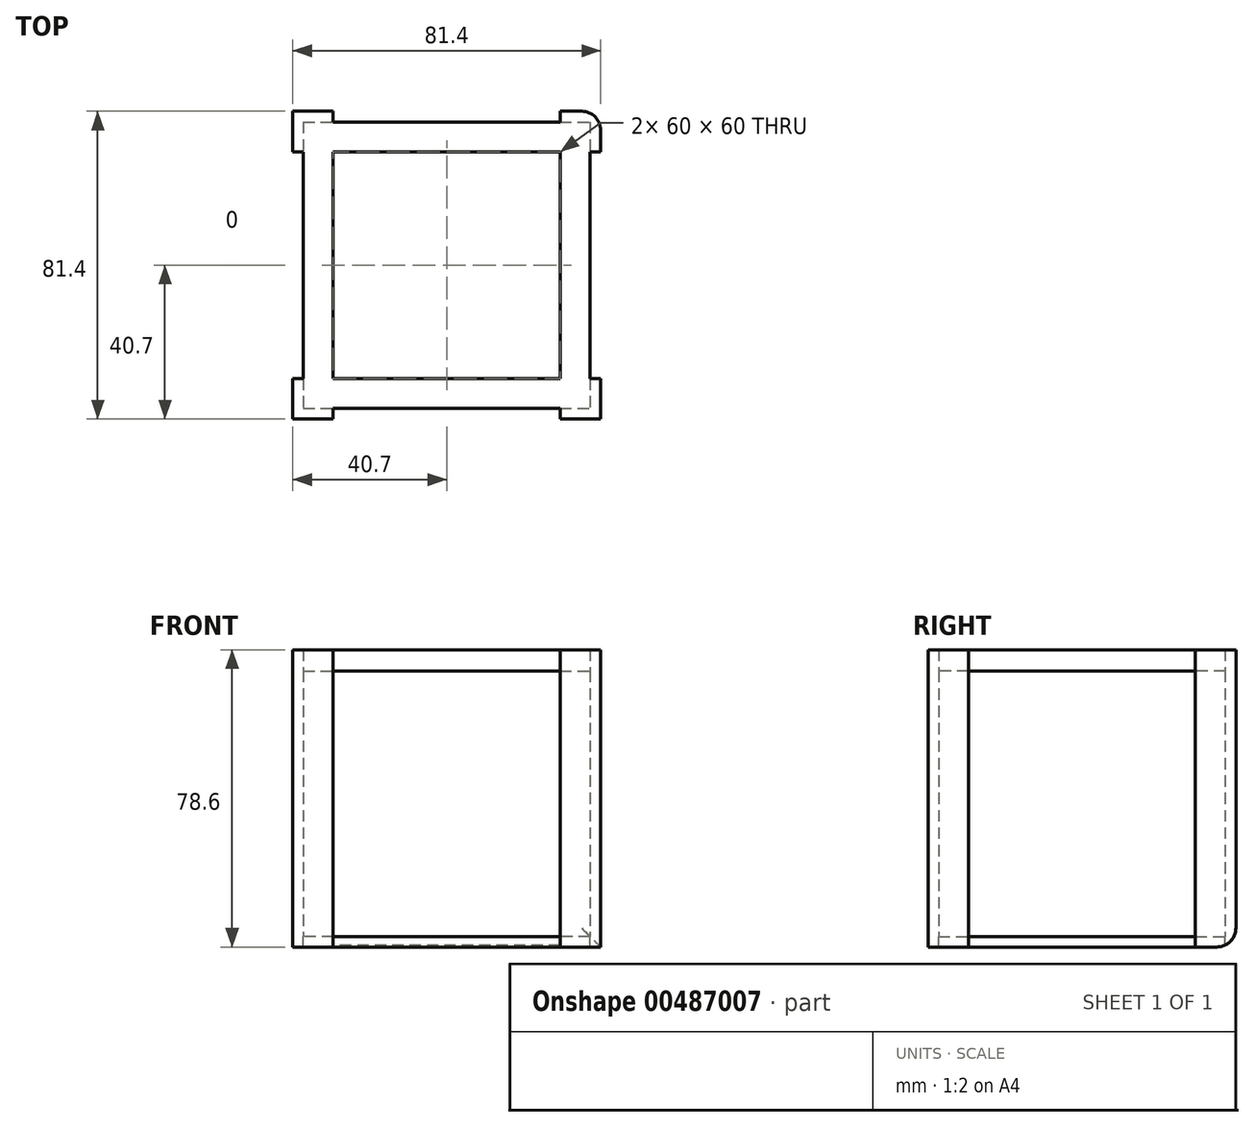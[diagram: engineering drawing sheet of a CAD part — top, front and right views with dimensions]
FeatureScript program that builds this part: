
annotation { "Feature Type Name" : "Feature", "Feature Type Description" : "" }
export const myFeature = defineFeature(function(context is Context, id is Id, definition is map)
    precondition{}
    {
        {
            var Q0;
            Q0=qCreatedBy(makeId("Top.planeOp"),FACE);
            var sketch = newSketch(context, id + "F0", { "sketchPlane" : qUnion([Q0])});
            skLineSegment(sketch, "E0.bottom", {"start": v(37.9, -37.9) * mm, "end": v(-37.9, -37.9) * mm});
            skLineSegment(sketch, "E0.top", {"start": v(37.9, 37.9) * mm, "end": v(-37.9, 37.9) * mm});
            skLineSegment(sketch, "E0.left", {"start": v(37.9, -37.9) * mm, "end": v(37.9, 37.9) * mm});
            skLineSegment(sketch, "E0.right", {"start": v(-37.9, -37.9) * mm, "end": v(-37.9, 37.9) * mm});
            skPoint(sketch, "E0.middle", {"position": v(0, 0) * mm});
            skLineSegment(sketch, "E1.0", {"start": v(40.7, 40.7) * mm, "end": v(-40.7, 40.7) * mm});
            skLineSegment(sketch, "E1.1", {"start": v(40.7, -40.7) * mm, "end": v(40.7, 40.7) * mm});
            skLineSegment(sketch, "E1.2", {"start": v(40.7, -40.7) * mm, "end": v(-40.7, -40.7) * mm});
            skLineSegment(sketch, "E1.3", {"start": v(-40.7, -40.7) * mm, "end": v(-40.7, 40.7) * mm});
            skLineSegment(sketch, "E2.bottom", {"start": v(-30, 40.7) * mm, "end": v(30, 40.7) * mm});
            skLineSegment(sketch, "E2.top", {"start": v(-30, -40.7) * mm, "end": v(30, -40.7) * mm});
            skLineSegment(sketch, "E2.left", {"start": v(-30, 40.7) * mm, "end": v(-30, -40.7) * mm});
            skLineSegment(sketch, "E2.right", {"start": v(30, 40.7) * mm, "end": v(30, -40.7) * mm});
            skLineSegment(sketch, "E3.bottom", {"start": v(-40.7, 30) * mm, "end": v(40.7, 30) * mm});
            skLineSegment(sketch, "E3.top", {"start": v(-40.7, -30) * mm, "end": v(40.7, -30) * mm});
            skLineSegment(sketch, "E3.left", {"start": v(-40.7, 30) * mm, "end": v(-40.7, -30) * mm});
            skLineSegment(sketch, "E3.right", {"start": v(40.7, 30) * mm, "end": v(40.7, -30) * mm});
            skSolve(sketch);
        }
        {
            var Q0;
            {var subQ5=sQuery(id+"F0.wireOp",EDGE,"E2.bottom");Q0=makeQuery(id+"F0.imprint","IMPRINT",FACE,{"disambiguationData":[TD([[makeQuery(id+"F0.imprint","IMPRINT",EDGE,{"derivedFrom":subQ5}),-1.0]])]});}
            var Q1;
            {var subQ7=sQuery(id+"F0.wireOp",EDGE,"E0.right");var subQ8=sQuery(id+"F0.wireOp",EDGE,"E0.top");var subQ9=makeQuery(id+"F0.imprint","INTERSECT",VERTEX,{"derivedFrom":[subQ8,subQ7]});Q1=makeQuery(id+"F0.imprint","IMPRINT",FACE,{"disambiguationData":[TD([[makeQuery(id+"F0.imprint","IMPRINT",EDGE,{"disambiguationData":[TD([[subQ9,1.0]])],"derivedFrom":subQ8}),-1.0]])]});}
            var Q2;
            {var subQ7=sQuery(id+"F0.wireOp",EDGE,"E0.left");var subQ8=sQuery(id+"F0.wireOp",EDGE,"E0.top");var subQ9=makeQuery(id+"F0.imprint","INTERSECT",VERTEX,{"derivedFrom":[subQ8,subQ7]});Q2=makeQuery(id+"F0.imprint","IMPRINT",FACE,{"disambiguationData":[TD([[makeQuery(id+"F0.imprint","IMPRINT",EDGE,{"disambiguationData":[TD([[subQ9,-1.0]])],"derivedFrom":subQ8}),-1.0]])]});}
            var Q3;
            {var subQ5=sQuery(id+"F0.wireOp",EDGE,"E3.right");Q3=makeQuery(id+"F0.imprint","IMPRINT",FACE,{"disambiguationData":[TD([[makeQuery(id+"F0.imprint","IMPRINT",EDGE,{"derivedFrom":subQ5}),-1.0]])]});}
            var Q4;
            {var subQ7=sQuery(id+"F0.wireOp",EDGE,"E0.left");var subQ8=sQuery(id+"F0.wireOp",EDGE,"E0.bottom");var subQ9=makeQuery(id+"F0.imprint","INTERSECT",VERTEX,{"derivedFrom":[subQ8,subQ7]});Q4=makeQuery(id+"F0.imprint","IMPRINT",FACE,{"disambiguationData":[TD([[makeQuery(id+"F0.imprint","IMPRINT",EDGE,{"disambiguationData":[TD([[subQ9,-1.0]])],"derivedFrom":subQ8}),1.0]])]});}
            var Q5;
            {var subQ5=sQuery(id+"F0.wireOp",EDGE,"E2.top");Q5=makeQuery(id+"F0.imprint","IMPRINT",FACE,{"disambiguationData":[TD([[makeQuery(id+"F0.imprint","IMPRINT",EDGE,{"derivedFrom":subQ5}),1.0]])]});}
            var Q6;
            {var subQ5=sQuery(id+"F0.wireOp",EDGE,"E0.right");var subQ6=sQuery(id+"F0.wireOp",EDGE,"E0.bottom");var subQ7=makeQuery(id+"F0.imprint","INTERSECT",VERTEX,{"derivedFrom":[subQ6,subQ5]});Q6=makeQuery(id+"F0.imprint","IMPRINT",FACE,{"disambiguationData":[TD([[makeQuery(id+"F0.imprint","IMPRINT",EDGE,{"disambiguationData":[TD([[subQ7,1.0]])],"derivedFrom":subQ6}),1.0]])]});}
            var Q7;
            {var subQ5=sQuery(id+"F0.wireOp",EDGE,"E3.left");Q7=makeQuery(id+"F0.imprint","IMPRINT",FACE,{"disambiguationData":[TD([[makeQuery(id+"F0.imprint","IMPRINT",EDGE,{"derivedFrom":subQ5}),1.0]])]});}
            var Q8;
            {var subQ0=sQuery(id+"F0.wireOp",EDGE,"E0.left");var subQ1=sQuery(id+"F0.wireOp",EDGE,"E0.bottom");var subQ2=makeQuery(id+"F0.imprint","INTERSECT",VERTEX,{"derivedFrom":[subQ1,subQ0]});Q8=makeQuery(id+"F0.imprint","IMPRINT",FACE,{"disambiguationData":[TD([[makeQuery(id+"F0.imprint","IMPRINT",EDGE,{"disambiguationData":[TD([[subQ2,-1.0]])],"derivedFrom":subQ1}),-1.0]])]});}
            var Q9;
            {var subQ0=sQuery(id+"F0.wireOp",EDGE,"E0.left");var subQ1=sQuery(id+"F0.wireOp",EDGE,"E0.top");var subQ2=makeQuery(id+"F0.imprint","INTERSECT",VERTEX,{"derivedFrom":[subQ1,subQ0]});Q9=makeQuery(id+"F0.imprint","IMPRINT",FACE,{"disambiguationData":[TD([[makeQuery(id+"F0.imprint","IMPRINT",EDGE,{"disambiguationData":[TD([[subQ2,-1.0]])],"derivedFrom":subQ1}),1.0]])]});}
            var Q10;
            {var subQ0=sQuery(id+"F0.wireOp",EDGE,"E0.right");var subQ1=sQuery(id+"F0.wireOp",EDGE,"E0.top");var subQ2=makeQuery(id+"F0.imprint","INTERSECT",VERTEX,{"derivedFrom":[subQ1,subQ0]});Q10=makeQuery(id+"F0.imprint","IMPRINT",FACE,{"disambiguationData":[TD([[makeQuery(id+"F0.imprint","IMPRINT",EDGE,{"disambiguationData":[TD([[subQ2,1.0]])],"derivedFrom":subQ1}),1.0]])]});}
            var Q11;
            {var subQ0=sQuery(id+"F0.wireOp",EDGE,"E3.top");var subQ1=sQuery(id+"F0.wireOp",EDGE,"E0.right");var subQ2=makeQuery(id+"F0.imprint","INTERSECT",VERTEX,{"derivedFrom":[subQ1,subQ0]});Q11=makeQuery(id+"F0.imprint","IMPRINT",FACE,{"disambiguationData":[TD([[makeQuery(id+"F0.imprint","IMPRINT",EDGE,{"disambiguationData":[TD([[subQ2,-1.0]])],"derivedFrom":subQ1}),-1.0]])]});}
            var Q12;
            {var subQ0=sQuery(id+"F0.wireOp",EDGE,"E3.top");var subQ1=sQuery(id+"F0.wireOp",EDGE,"E0.left");var subQ2=makeQuery(id+"F0.imprint","INTERSECT",VERTEX,{"derivedFrom":[subQ1,subQ0]});Q12=makeQuery(id+"F0.imprint","IMPRINT",FACE,{"disambiguationData":[TD([[makeQuery(id+"F0.imprint","IMPRINT",EDGE,{"disambiguationData":[TD([[subQ2,-1.0]])],"derivedFrom":subQ1}),1.0]])]});}
            var Q13;
            {var subQ0=sQuery(id+"F0.wireOp",EDGE,"E0.right");var subQ1=sQuery(id+"F0.wireOp",EDGE,"E0.bottom");var subQ2=makeQuery(id+"F0.imprint","INTERSECT",VERTEX,{"derivedFrom":[subQ1,subQ0]});Q13=makeQuery(id+"F0.imprint","IMPRINT",FACE,{"disambiguationData":[TD([[makeQuery(id+"F0.imprint","IMPRINT",EDGE,{"disambiguationData":[TD([[subQ2,1.0]])],"derivedFrom":subQ1}),-1.0]])]});}
            var Q14;
            {var subQ0=sQuery(id+"F0.wireOp",EDGE,"E2.right");var subQ1=sQuery(id+"F0.wireOp",EDGE,"E0.bottom");var subQ2=makeQuery(id+"F0.imprint","INTERSECT",VERTEX,{"derivedFrom":[subQ1,subQ0]});Q14=makeQuery(id+"F0.imprint","IMPRINT",FACE,{"disambiguationData":[TD([[makeQuery(id+"F0.imprint","IMPRINT",EDGE,{"disambiguationData":[TD([[subQ2,-1.0]])],"derivedFrom":subQ1}),-1.0]])]});}
            var Q15;
            {var subQ0=sQuery(id+"F0.wireOp",EDGE,"E2.right");var subQ1=sQuery(id+"F0.wireOp",EDGE,"E0.top");var subQ2=makeQuery(id+"F0.imprint","INTERSECT",VERTEX,{"derivedFrom":[subQ1,subQ0]});Q15=makeQuery(id+"F0.imprint","IMPRINT",FACE,{"disambiguationData":[TD([[makeQuery(id+"F0.imprint","IMPRINT",EDGE,{"disambiguationData":[TD([[subQ2,-1.0]])],"derivedFrom":subQ1}),1.0]])]});}
            extrude(context, id + "F1", {"entities" : qUnion([Q0, Q1, Q2, Q3, Q4, Q5, Q6, Q7, Q8, Q9, Q10, Q11, Q12, Q13, Q14, Q15]), "depth" : 75.8 * mm});
        }
        {
            var Q0;
            {var subQ7=sQuery(id+"F0.wireOp",EDGE,"E0.right");var subQ8=sQuery(id+"F0.wireOp",EDGE,"E0.top");var subQ9=makeQuery(id+"F0.imprint","INTERSECT",VERTEX,{"derivedFrom":[subQ8,subQ7]});Q0=makeQuery(id+"F0.imprint","IMPRINT",FACE,{"disambiguationData":[TD([[makeQuery(id+"F0.imprint","IMPRINT",EDGE,{"disambiguationData":[TD([[subQ9,1.0]])],"derivedFrom":subQ8}),-1.0]])]});}
            var Q1;
            {var subQ0=sQuery(id+"F0.wireOp",EDGE,"E0.right");var subQ1=sQuery(id+"F0.wireOp",EDGE,"E0.top");var subQ2=makeQuery(id+"F0.imprint","INTERSECT",VERTEX,{"derivedFrom":[subQ1,subQ0]});Q1=makeQuery(id+"F0.imprint","IMPRINT",FACE,{"disambiguationData":[TD([[makeQuery(id+"F0.imprint","IMPRINT",EDGE,{"disambiguationData":[TD([[subQ2,1.0]])],"derivedFrom":subQ1}),1.0]])]});}
            var Q2;
            {var subQ5=sQuery(id+"F0.wireOp",EDGE,"E3.left");Q2=makeQuery(id+"F0.imprint","IMPRINT",FACE,{"disambiguationData":[TD([[makeQuery(id+"F0.imprint","IMPRINT",EDGE,{"derivedFrom":subQ5}),1.0]])]});}
            var Q3;
            {var subQ0=sQuery(id+"F0.wireOp",EDGE,"E3.top");var subQ1=sQuery(id+"F0.wireOp",EDGE,"E0.right");var subQ2=makeQuery(id+"F0.imprint","INTERSECT",VERTEX,{"derivedFrom":[subQ1,subQ0]});Q3=makeQuery(id+"F0.imprint","IMPRINT",FACE,{"disambiguationData":[TD([[makeQuery(id+"F0.imprint","IMPRINT",EDGE,{"disambiguationData":[TD([[subQ2,-1.0]])],"derivedFrom":subQ1}),-1.0]])]});}
            var Q4;
            {var subQ5=sQuery(id+"F0.wireOp",EDGE,"E0.right");var subQ6=sQuery(id+"F0.wireOp",EDGE,"E0.bottom");var subQ7=makeQuery(id+"F0.imprint","INTERSECT",VERTEX,{"derivedFrom":[subQ6,subQ5]});Q4=makeQuery(id+"F0.imprint","IMPRINT",FACE,{"disambiguationData":[TD([[makeQuery(id+"F0.imprint","IMPRINT",EDGE,{"disambiguationData":[TD([[subQ7,1.0]])],"derivedFrom":subQ6}),1.0]])]});}
            var Q5;
            {var subQ0=sQuery(id+"F0.wireOp",EDGE,"E0.right");var subQ1=sQuery(id+"F0.wireOp",EDGE,"E0.bottom");var subQ2=makeQuery(id+"F0.imprint","INTERSECT",VERTEX,{"derivedFrom":[subQ1,subQ0]});Q5=makeQuery(id+"F0.imprint","IMPRINT",FACE,{"disambiguationData":[TD([[makeQuery(id+"F0.imprint","IMPRINT",EDGE,{"disambiguationData":[TD([[subQ2,1.0]])],"derivedFrom":subQ1}),-1.0]])]});}
            var Q6;
            {var subQ5=sQuery(id+"F0.wireOp",EDGE,"E2.top");Q6=makeQuery(id+"F0.imprint","IMPRINT",FACE,{"disambiguationData":[TD([[makeQuery(id+"F0.imprint","IMPRINT",EDGE,{"derivedFrom":subQ5}),1.0]])]});}
            var Q7;
            {var subQ0=sQuery(id+"F0.wireOp",EDGE,"E0.left");var subQ1=sQuery(id+"F0.wireOp",EDGE,"E0.bottom");var subQ2=makeQuery(id+"F0.imprint","INTERSECT",VERTEX,{"derivedFrom":[subQ1,subQ0]});Q7=makeQuery(id+"F0.imprint","IMPRINT",FACE,{"disambiguationData":[TD([[makeQuery(id+"F0.imprint","IMPRINT",EDGE,{"disambiguationData":[TD([[subQ2,-1.0]])],"derivedFrom":subQ1}),-1.0]])]});}
            var Q8;
            {var subQ0=sQuery(id+"F0.wireOp",EDGE,"E3.top");var subQ1=sQuery(id+"F0.wireOp",EDGE,"E0.left");var subQ2=makeQuery(id+"F0.imprint","INTERSECT",VERTEX,{"derivedFrom":[subQ1,subQ0]});Q8=makeQuery(id+"F0.imprint","IMPRINT",FACE,{"disambiguationData":[TD([[makeQuery(id+"F0.imprint","IMPRINT",EDGE,{"disambiguationData":[TD([[subQ2,-1.0]])],"derivedFrom":subQ1}),1.0]])]});}
            var Q9;
            {var subQ0=sQuery(id+"F0.wireOp",EDGE,"E0.left");var subQ1=sQuery(id+"F0.wireOp",EDGE,"E0.top");var subQ2=makeQuery(id+"F0.imprint","INTERSECT",VERTEX,{"derivedFrom":[subQ1,subQ0]});Q9=makeQuery(id+"F0.imprint","IMPRINT",FACE,{"disambiguationData":[TD([[makeQuery(id+"F0.imprint","IMPRINT",EDGE,{"disambiguationData":[TD([[subQ2,-1.0]])],"derivedFrom":subQ1}),1.0]])]});}
            var Q10;
            {var subQ0=sQuery(id+"F0.wireOp",EDGE,"E2.right");var subQ1=sQuery(id+"F0.wireOp",EDGE,"E0.top");var subQ2=makeQuery(id+"F0.imprint","INTERSECT",VERTEX,{"derivedFrom":[subQ1,subQ0]});Q10=makeQuery(id+"F0.imprint","IMPRINT",FACE,{"disambiguationData":[TD([[makeQuery(id+"F0.imprint","IMPRINT",EDGE,{"disambiguationData":[TD([[subQ2,-1.0]])],"derivedFrom":subQ1}),1.0]])]});}
            var Q11;
            {var subQ5=sQuery(id+"F0.wireOp",EDGE,"E2.bottom");Q11=makeQuery(id+"F0.imprint","IMPRINT",FACE,{"disambiguationData":[TD([[makeQuery(id+"F0.imprint","IMPRINT",EDGE,{"derivedFrom":subQ5}),-1.0]])]});}
            var Q12;
            {var subQ7=sQuery(id+"F0.wireOp",EDGE,"E0.left");var subQ8=sQuery(id+"F0.wireOp",EDGE,"E0.top");var subQ9=makeQuery(id+"F0.imprint","INTERSECT",VERTEX,{"derivedFrom":[subQ8,subQ7]});Q12=makeQuery(id+"F0.imprint","IMPRINT",FACE,{"disambiguationData":[TD([[makeQuery(id+"F0.imprint","IMPRINT",EDGE,{"disambiguationData":[TD([[subQ9,-1.0]])],"derivedFrom":subQ8}),-1.0]])]});}
            var Q13;
            {var subQ5=sQuery(id+"F0.wireOp",EDGE,"E3.right");Q13=makeQuery(id+"F0.imprint","IMPRINT",FACE,{"disambiguationData":[TD([[makeQuery(id+"F0.imprint","IMPRINT",EDGE,{"derivedFrom":subQ5}),-1.0]])]});}
            var Q14;
            {var subQ7=sQuery(id+"F0.wireOp",EDGE,"E0.left");var subQ8=sQuery(id+"F0.wireOp",EDGE,"E0.bottom");var subQ9=makeQuery(id+"F0.imprint","INTERSECT",VERTEX,{"derivedFrom":[subQ8,subQ7]});Q14=makeQuery(id+"F0.imprint","IMPRINT",FACE,{"disambiguationData":[TD([[makeQuery(id+"F0.imprint","IMPRINT",EDGE,{"disambiguationData":[TD([[subQ9,-1.0]])],"derivedFrom":subQ8}),1.0]])]});}
            var Q15;
            {var subQ0=sQuery(id+"F0.wireOp",EDGE,"E2.right");var subQ1=sQuery(id+"F0.wireOp",EDGE,"E0.bottom");var subQ2=makeQuery(id+"F0.imprint","INTERSECT",VERTEX,{"derivedFrom":[subQ1,subQ0]});Q15=makeQuery(id+"F0.imprint","IMPRINT",FACE,{"disambiguationData":[TD([[makeQuery(id+"F0.imprint","IMPRINT",EDGE,{"disambiguationData":[TD([[subQ2,-1.0]])],"derivedFrom":subQ1}),-1.0]])]});}
            extrude(context, id + "F2", {"entities" : qUnion([Q0, Q1, Q2, Q3, Q4, Q5, Q6, Q7, Q8, Q9, Q10, Q11, Q12, Q13, Q14, Q15]), "operationType" : NewBodyOperationType.REMOVE, "depth" : (75.8 - 5.6) * mm});
        }
        {
            var Q0;
            {var subQ5=sQuery(id+"F0.wireOp",EDGE,"E0.right");var subQ6=sQuery(id+"F0.wireOp",EDGE,"E0.bottom");var subQ7=makeQuery(id+"F0.imprint","INTERSECT",VERTEX,{"derivedFrom":[subQ6,subQ5]});Q0=makeQuery(id+"F0.imprint","IMPRINT",FACE,{"disambiguationData":[TD([[makeQuery(id+"F0.imprint","IMPRINT",EDGE,{"disambiguationData":[TD([[subQ7,1.0]])],"derivedFrom":subQ6}),1.0]])]});}
            var Q1;
            {var subQ7=sQuery(id+"F0.wireOp",EDGE,"E0.left");var subQ8=sQuery(id+"F0.wireOp",EDGE,"E0.bottom");var subQ9=makeQuery(id+"F0.imprint","INTERSECT",VERTEX,{"derivedFrom":[subQ8,subQ7]});Q1=makeQuery(id+"F0.imprint","IMPRINT",FACE,{"disambiguationData":[TD([[makeQuery(id+"F0.imprint","IMPRINT",EDGE,{"disambiguationData":[TD([[subQ9,-1.0]])],"derivedFrom":subQ8}),1.0]])]});}
            var Q2;
            {var subQ7=sQuery(id+"F0.wireOp",EDGE,"E0.left");var subQ8=sQuery(id+"F0.wireOp",EDGE,"E0.top");var subQ9=makeQuery(id+"F0.imprint","INTERSECT",VERTEX,{"derivedFrom":[subQ8,subQ7]});Q2=makeQuery(id+"F0.imprint","IMPRINT",FACE,{"disambiguationData":[TD([[makeQuery(id+"F0.imprint","IMPRINT",EDGE,{"disambiguationData":[TD([[subQ9,-1.0]])],"derivedFrom":subQ8}),-1.0]])]});}
            var Q3;
            {var subQ7=sQuery(id+"F0.wireOp",EDGE,"E0.right");var subQ8=sQuery(id+"F0.wireOp",EDGE,"E0.top");var subQ9=makeQuery(id+"F0.imprint","INTERSECT",VERTEX,{"derivedFrom":[subQ8,subQ7]});Q3=makeQuery(id+"F0.imprint","IMPRINT",FACE,{"disambiguationData":[TD([[makeQuery(id+"F0.imprint","IMPRINT",EDGE,{"disambiguationData":[TD([[subQ9,1.0]])],"derivedFrom":subQ8}),-1.0]])]});}
            extrude(context, id + "F3", {"entities" : qUnion([Q0, Q1, Q2, Q3]), "operationType" : NewBodyOperationType.ADD, "depth" : 75.8 * mm});
        }
        {
            var Q0;
            {var subQ5=sQuery(id+"F0.wireOp",EDGE,"E0.right");var subQ6=sQuery(id+"F0.wireOp",EDGE,"E0.bottom");var subQ7=makeQuery(id+"F0.imprint","INTERSECT",VERTEX,{"derivedFrom":[subQ6,subQ5]});Q0=makeQuery(id+"F0.imprint","IMPRINT",FACE,{"disambiguationData":[TD([[makeQuery(id+"F0.imprint","IMPRINT",EDGE,{"disambiguationData":[TD([[subQ7,1.0]])],"derivedFrom":subQ6}),1.0]])]});}
            var Q1;
            {var subQ0=sQuery(id+"F0.wireOp",EDGE,"E0.right");var subQ1=sQuery(id+"F0.wireOp",EDGE,"E0.bottom");var subQ2=makeQuery(id+"F0.imprint","INTERSECT",VERTEX,{"derivedFrom":[subQ1,subQ0]});Q1=makeQuery(id+"F0.imprint","IMPRINT",FACE,{"disambiguationData":[TD([[makeQuery(id+"F0.imprint","IMPRINT",EDGE,{"disambiguationData":[TD([[subQ2,1.0]])],"derivedFrom":subQ1}),-1.0]])]});}
            var Q2;
            {var subQ0=sQuery(id+"F0.wireOp",EDGE,"E2.right");var subQ1=sQuery(id+"F0.wireOp",EDGE,"E0.bottom");var subQ2=makeQuery(id+"F0.imprint","INTERSECT",VERTEX,{"derivedFrom":[subQ1,subQ0]});Q2=makeQuery(id+"F0.imprint","IMPRINT",FACE,{"disambiguationData":[TD([[makeQuery(id+"F0.imprint","IMPRINT",EDGE,{"disambiguationData":[TD([[subQ2,-1.0]])],"derivedFrom":subQ1}),-1.0]])]});}
            var Q3;
            {var subQ5=sQuery(id+"F0.wireOp",EDGE,"E2.top");Q3=makeQuery(id+"F0.imprint","IMPRINT",FACE,{"disambiguationData":[TD([[makeQuery(id+"F0.imprint","IMPRINT",EDGE,{"derivedFrom":subQ5}),1.0]])]});}
            var Q4;
            {var subQ7=sQuery(id+"F0.wireOp",EDGE,"E0.left");var subQ8=sQuery(id+"F0.wireOp",EDGE,"E0.bottom");var subQ9=makeQuery(id+"F0.imprint","INTERSECT",VERTEX,{"derivedFrom":[subQ8,subQ7]});Q4=makeQuery(id+"F0.imprint","IMPRINT",FACE,{"disambiguationData":[TD([[makeQuery(id+"F0.imprint","IMPRINT",EDGE,{"disambiguationData":[TD([[subQ9,-1.0]])],"derivedFrom":subQ8}),1.0]])]});}
            var Q5;
            {var subQ0=sQuery(id+"F0.wireOp",EDGE,"E0.left");var subQ1=sQuery(id+"F0.wireOp",EDGE,"E0.bottom");var subQ2=makeQuery(id+"F0.imprint","INTERSECT",VERTEX,{"derivedFrom":[subQ1,subQ0]});Q5=makeQuery(id+"F0.imprint","IMPRINT",FACE,{"disambiguationData":[TD([[makeQuery(id+"F0.imprint","IMPRINT",EDGE,{"disambiguationData":[TD([[subQ2,-1.0]])],"derivedFrom":subQ1}),-1.0]])]});}
            var Q6;
            {var subQ5=sQuery(id+"F0.wireOp",EDGE,"E3.right");Q6=makeQuery(id+"F0.imprint","IMPRINT",FACE,{"disambiguationData":[TD([[makeQuery(id+"F0.imprint","IMPRINT",EDGE,{"derivedFrom":subQ5}),-1.0]])]});}
            var Q7;
            {var subQ0=sQuery(id+"F0.wireOp",EDGE,"E3.top");var subQ1=sQuery(id+"F0.wireOp",EDGE,"E0.left");var subQ2=makeQuery(id+"F0.imprint","INTERSECT",VERTEX,{"derivedFrom":[subQ1,subQ0]});Q7=makeQuery(id+"F0.imprint","IMPRINT",FACE,{"disambiguationData":[TD([[makeQuery(id+"F0.imprint","IMPRINT",EDGE,{"disambiguationData":[TD([[subQ2,-1.0]])],"derivedFrom":subQ1}),1.0]])]});}
            var Q8;
            {var subQ0=sQuery(id+"F0.wireOp",EDGE,"E0.left");var subQ1=sQuery(id+"F0.wireOp",EDGE,"E0.top");var subQ2=makeQuery(id+"F0.imprint","INTERSECT",VERTEX,{"derivedFrom":[subQ1,subQ0]});Q8=makeQuery(id+"F0.imprint","IMPRINT",FACE,{"disambiguationData":[TD([[makeQuery(id+"F0.imprint","IMPRINT",EDGE,{"disambiguationData":[TD([[subQ2,-1.0]])],"derivedFrom":subQ1}),1.0]])]});}
            var Q9;
            {var subQ7=sQuery(id+"F0.wireOp",EDGE,"E0.left");var subQ8=sQuery(id+"F0.wireOp",EDGE,"E0.top");var subQ9=makeQuery(id+"F0.imprint","INTERSECT",VERTEX,{"derivedFrom":[subQ8,subQ7]});Q9=makeQuery(id+"F0.imprint","IMPRINT",FACE,{"disambiguationData":[TD([[makeQuery(id+"F0.imprint","IMPRINT",EDGE,{"disambiguationData":[TD([[subQ9,-1.0]])],"derivedFrom":subQ8}),-1.0]])]});}
            var Q10;
            {var subQ0=sQuery(id+"F0.wireOp",EDGE,"E2.right");var subQ1=sQuery(id+"F0.wireOp",EDGE,"E0.top");var subQ2=makeQuery(id+"F0.imprint","INTERSECT",VERTEX,{"derivedFrom":[subQ1,subQ0]});Q10=makeQuery(id+"F0.imprint","IMPRINT",FACE,{"disambiguationData":[TD([[makeQuery(id+"F0.imprint","IMPRINT",EDGE,{"disambiguationData":[TD([[subQ2,-1.0]])],"derivedFrom":subQ1}),1.0]])]});}
            var Q11;
            {var subQ5=sQuery(id+"F0.wireOp",EDGE,"E2.bottom");Q11=makeQuery(id+"F0.imprint","IMPRINT",FACE,{"disambiguationData":[TD([[makeQuery(id+"F0.imprint","IMPRINT",EDGE,{"derivedFrom":subQ5}),-1.0]])]});}
            var Q12;
            {var subQ0=sQuery(id+"F0.wireOp",EDGE,"E0.right");var subQ1=sQuery(id+"F0.wireOp",EDGE,"E0.top");var subQ2=makeQuery(id+"F0.imprint","INTERSECT",VERTEX,{"derivedFrom":[subQ1,subQ0]});Q12=makeQuery(id+"F0.imprint","IMPRINT",FACE,{"disambiguationData":[TD([[makeQuery(id+"F0.imprint","IMPRINT",EDGE,{"disambiguationData":[TD([[subQ2,1.0]])],"derivedFrom":subQ1}),1.0]])]});}
            var Q13;
            {var subQ7=sQuery(id+"F0.wireOp",EDGE,"E0.right");var subQ8=sQuery(id+"F0.wireOp",EDGE,"E0.top");var subQ9=makeQuery(id+"F0.imprint","INTERSECT",VERTEX,{"derivedFrom":[subQ8,subQ7]});Q13=makeQuery(id+"F0.imprint","IMPRINT",FACE,{"disambiguationData":[TD([[makeQuery(id+"F0.imprint","IMPRINT",EDGE,{"disambiguationData":[TD([[subQ9,1.0]])],"derivedFrom":subQ8}),-1.0]])]});}
            var Q14;
            {var subQ5=sQuery(id+"F0.wireOp",EDGE,"E3.left");Q14=makeQuery(id+"F0.imprint","IMPRINT",FACE,{"disambiguationData":[TD([[makeQuery(id+"F0.imprint","IMPRINT",EDGE,{"derivedFrom":subQ5}),1.0]])]});}
            var Q15;
            {var subQ0=sQuery(id+"F0.wireOp",EDGE,"E3.top");var subQ1=sQuery(id+"F0.wireOp",EDGE,"E0.right");var subQ2=makeQuery(id+"F0.imprint","INTERSECT",VERTEX,{"derivedFrom":[subQ1,subQ0]});Q15=makeQuery(id+"F0.imprint","IMPRINT",FACE,{"disambiguationData":[TD([[makeQuery(id+"F0.imprint","IMPRINT",EDGE,{"disambiguationData":[TD([[subQ2,-1.0]])],"derivedFrom":subQ1}),-1.0]])]});}
            extrude(context, id + "F4", {"entities" : qUnion([Q0, Q1, Q2, Q3, Q4, Q5, Q6, Q7, Q8, Q9, Q10, Q11, Q12, Q13, Q14, Q15]), "operationType" : NewBodyOperationType.ADD, "oppositeDirection" : true, "depth" : 2.8 * mm});
        }
        {
            var Q0;
            Q0=makeQuery(id+"F4.opExtrude","CAP_EDGE",EDGE,{"disambiguationData":[OSD([sQuery(id+"F0.wireOp",EDGE,"E1.0"),sQuery(id+"F0.wireOp",EDGE,"E2.bottom")])],"isStart":false});
            var Q1;
            {var subQ0=sQuery(id+"F0.wireOp",EDGE,"E1.1");var subQ1=sQuery(id+"F0.wireOp",EDGE,"E1.0");Q1=makeQuery(id+"F4.boolean.opBoolean","MERGE",EDGE,{"derivedFrom":[makeQuery(id+"F3.boolean.opBoolean","MERGE",EDGE,{"derivedFrom":[makeQuery(id+"F1.opExtrude","SWEPT_EDGE",EDGE,{"disambiguationData":[OSD([subQ1,subQ0])]}),makeQuery(id+"F3.opExtrude","SWEPT_EDGE",EDGE,{"disambiguationData":[OSD([subQ1,subQ0])]})]}),makeQuery(id+"F4.opExtrude","SWEPT_EDGE",EDGE,{"disambiguationData":[OSD([subQ1,subQ0])]})]});}
            var Q2;
            {var subQ0=sQuery(id+"F0.wireOp",EDGE,"E3.top");Q2=makeQuery(id+"F3.opExtrude","CAP_EDGE",EDGE,{"disambiguationData":[OSD([subQ0]),TDD([makeQuery(id+"F0.imprint","IMPRINT",EDGE,{"disambiguationData":[TD([[makeQuery(id+"F0.imprint","INTERSECT",VERTEX,{"derivedFrom":[sQuery(id+"F0.wireOp",EDGE,"E0.left"),subQ0]}),-1.0]])],"derivedFrom":subQ0})])],"isStart":true});}
            fillet(context, id + "F5", {"entities" : qUnion([Q0, Q1, Q2]), "radius" : 5 * mm, "tangentPropagation" : true, "allowEdgeOverflow" : false});
        }
    });
